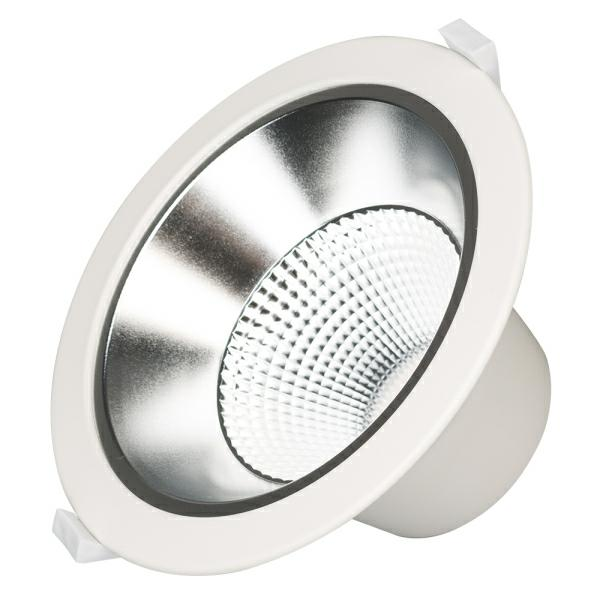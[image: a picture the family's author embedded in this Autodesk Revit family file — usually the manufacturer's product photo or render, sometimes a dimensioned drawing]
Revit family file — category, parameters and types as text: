
# Revit family: LEGEND-R115
name_source: partatom
category: Осветительные приборы
revit_build: Autodesk Revit 2017 (Build: 20160225_1515(x64)
units: mm (PartAtom-declared; Revit-internal decimal feet)

## family parameters
Источник света = Да
Общий = Нет
Основа = Грань
При загрузке вырезать с полостями = Нет
Размер круглого соединителя = Использовать диаметр
Тип детали = Нормальный
Точка расчета площади = Нет

## types (6) — shared parameters
ADSK_Единица измерения = шт.
ADSK_Завод-изготовитель = ARLIGHT
ADSK_Классификация нагрузок = Освещение
ADSK_Количество фаз = 1
ADSK_Количество фаз числовое = 1
ADSK_Коэффициент мощности = 0.91
ADSK_Масса_Текст = 0.3
ADSK_Наименование = Светильник
ADSK_Напряжение = 230 В
ADSK_Номинальная мощность = 10 Вт
ADSK_Полная мощность = 11 В·А
ADSK_Размер_Высота = 65.5 мм
ADSK_Размер_Диаметр = 113 мм
ADSK_Ток = 0 А
ARL_Драйвер = Встроенный (21-35V, 350mA)
ARL_Индекс цветопередачи = >80
ARL_Класс защиты от поражения электрическим током = III
ARL_Класс пылевлагозащиты = IP20
ARL_Материал корпуса = Металл, белый
ARL_Область использования = Для освещения торговых, офисных, жилых и других помещений
ARL_Обозначение корпуса = Корпус круглый, металл, цвет белый
ARL_Рабочая температура окружающей среды = -20...+40 °C
ARL_Серия = LEGEND
ARL_Способ монтажа = Встраиваемый
ARL_Тип товара = Светильник
ARL_Угол обзора = 50°
ARL_Цвет покрытия = Белый
URL = https://arlight.ru
Видимая форма излучения при визуализации = Нет
Группа модели = Светильники
Изготовитель = ARLIGHT
Изготовитель (сайт) = www.arlight.ru
Изготовитель (телефон) = 8 800 505 26 29
Излучение по диаметру окружности = 42 мм
Отметка по умолчанию = 1219.2 мм
Полная установленная мощность = 11 В·А
Разработчик = НТЦ Конструктор
Разработчик (URL) = https://constructor.ru
Разработчик (телефон) = +7 (495) 781-05-35
Светофильтр = 16777215
Смещение цветовой температуры при затухании лампы = <Нет>
Угол наклона = 90.00°

## per-type parameters (varying)
| type | ADSK_Код изделия | ADSK_Марка | ARL_Цвет свечения | Комментарии к типоразмеру | Описание | Файл фотометрической сетки |
| 027315 Светильник LTD-LEGEND-R115-10W White6000 (WH, 50 deg) | Арт. 027315 | LTD-LEGEND-R115-10W White6000 | Белый 6000K | Арт. 027315 | Встраиваемый светильник "Даунлайт" 10 Вт. Цвет свечения БЕЛЫЙ 6000К. Световой поток 880лм, угол 50°, CRI>80. Белый корпус. Питание AC220-240V. Габариты: Ø113х65.5 мм, врезное отверстие Ø90-102 мм. Драйвер в комплекте (21-35V, 350mA) | 027315_LTD-LEGEND-R115-10W White6000 (WH, 50 deg).ies |
| 027315(1) Светильник LTD-LEGEND-R115-10W White6000 (WH, 50 deg) | Арт. 027315(1) | LTD-LEGEND-R115-10W White6000 | Белый 6000K | Арт. 027315(1) | Встраиваемый светильник "Даунлайт" 10 Вт. Цвет свечения БЕЛЫЙ 6000К. Световой поток 880лм, угол 50°, CRI>80. Белый корпус. Питание AC220-240V. Габариты: Ø113х65.5 мм, врезное отверстие Ø90-102 мм. Драйвер в комплекте (18-35V, 350mA) | 027315 (1)_LTD-LEGEND-R115-10W White6000 (WH, 50 deg).ies |
| 027316 Светильник LTD-LEGEND-R115-10W Day4000 (WH, 50 deg) | Арт. 027316 | LTD-LEGEND-R115-10W Day4000 | Дневной 4000K | Арт. 027316 | Встраиваемый светильник "Даунлайт" 10 Вт. Цвет свечения ДНЕВНОЙ 4000К. Световой поток 880лм, угол 50°, CRI>80. Белый корпус. Питание AC220-240V. Габариты: Ø113х65.5 мм, врезное отверстие Ø90-102 мм. Драйвер в комплекте (21-35V, 350mA) | 027316_LTD-LEGEND-R115-10W Day4000 (WH, 50 deg).ies |
| 027316(1) Светильник LTD-LEGEND-R115-10W Day4000 (WH, 50 deg) | Арт. 027316(1) | LTD-LEGEND-R115-10W Day4000 | Дневной 4000K | Арт. 027316(1) | Встраиваемый светильник "Даунлайт" 10 Вт. Цвет свечения ДНЕВНОЙ 4000К. Световой поток 880лм, угол 50°, CRI>80. Белый корпус. Питание AC220-240V. Габариты: Ø113х65.5 мм, врезное отверстие Ø90-102 мм. Драйвер в комплекте (18-35V, 350mA) | 027316(1)_LTD-LEGEND-R115-10W Day4000 (WH, 50 deg).ies |
| 027317 Светильник LTD-LEGEND-R115-10W Warm3000 (WH, 50 deg) | Арт. 027317 | LTD-LEGEND-R115-10W Warm3000 | Теплый 3000K | Арт. 027317 | Встраиваемый светильник "Даунлайт" 10 Вт. Цвет свечения ТЕПЛЫЙ 3000К. Световой поток 800лм, угол 50°, CRI>80. Белый корпус. Питание AC220-240V. Габариты: Ø113х65.5 мм, врезное отверстие Ø90-102 мм. Драйвер в комплекте (21-35V, 350mA) | 027317_LTD-LEGEND-R115-10W Warm3000 (WH, 50 deg).ies |
| 027317(1) Светильник LTD-LEGEND-R115-10W Warm3000 (WH, 50 deg) | Арт. 027317(1) | LTD-LEGEND-R115-10W Warm3000 | Теплый 3000K | Арт. 027317(1) | Встраиваемый светильник "Даунлайт" 10 Вт. Цвет свечения ТЕПЛЫЙ 3000К. Световой поток 800лм, угол 50°, CRI>80. Белый корпус. Питание AC220-240V. Габариты: Ø113х65.5 мм, врезное отверстие Ø90-102 мм. Драйвер в комплекте (18-35V, 350mA) | 027317(1)_LTD-LEGEND-R115-10W Warm3000 (WH, 50 deg).ies |
